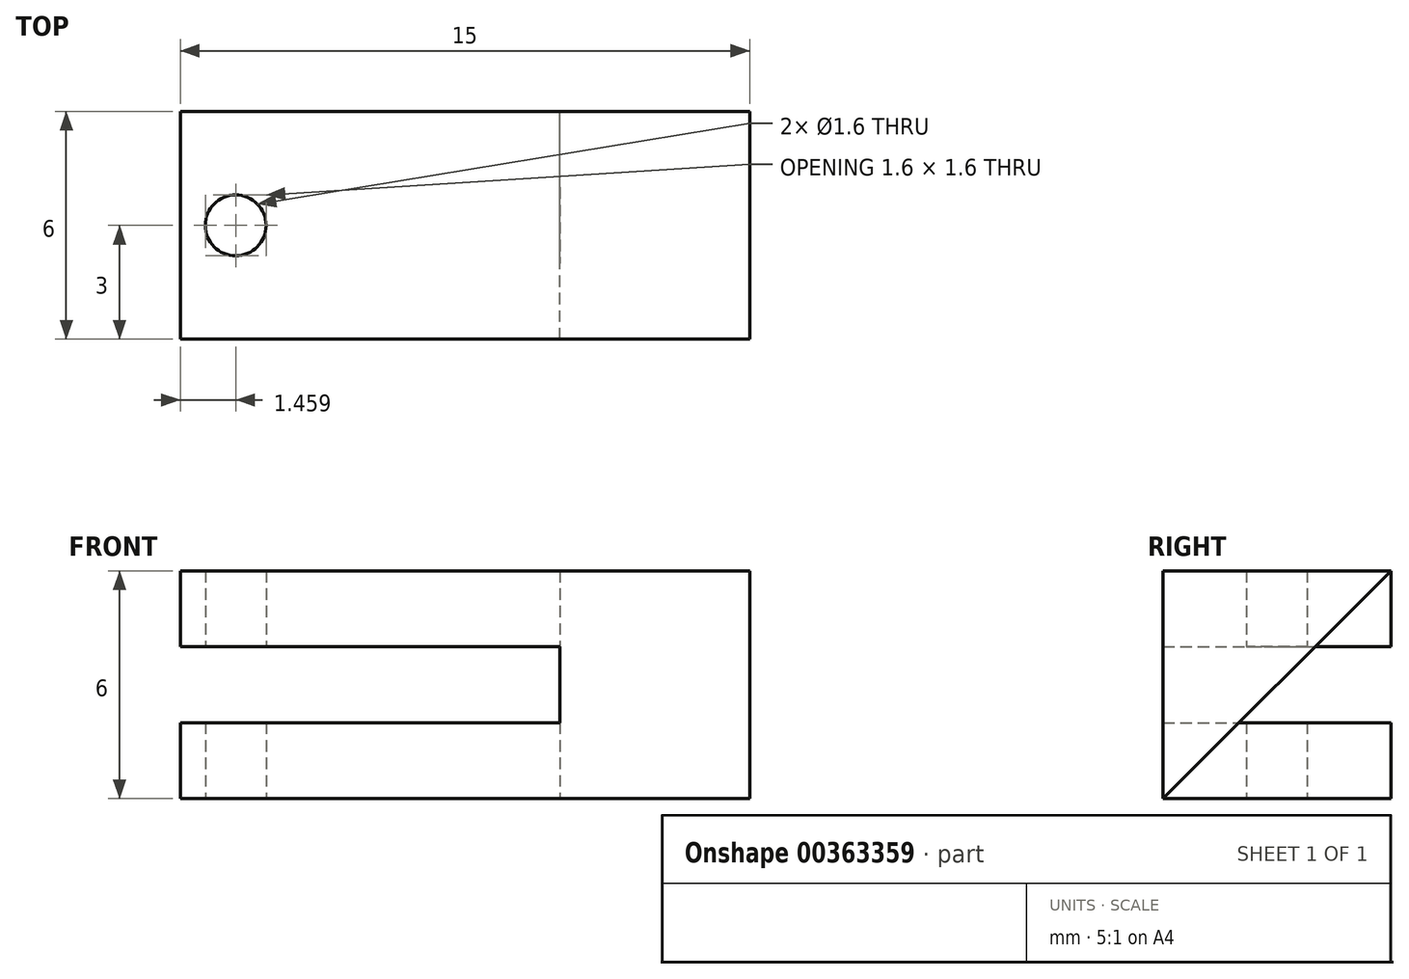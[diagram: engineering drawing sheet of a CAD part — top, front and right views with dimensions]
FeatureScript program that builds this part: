
annotation { "Feature Type Name" : "Feature", "Feature Type Description" : "" }
export const myFeature = defineFeature(function(context is Context, id is Id, definition is map)
    precondition{}
    {
        {
            var Q0;
            Q0=qCreatedBy(makeId("Front.planeOp"),FACE);
            var sketch = newSketch(context, id + "F0", { "sketchPlane" : qUnion([Q0])});
            skLineSegment(sketch, "E0", {"start": v(-77.64, 2.68) * mm, "end": v(-62.64, 2.68) * mm});
            skLineSegment(sketch, "E1", {"start": v(-62.64, 2.68) * mm, "end": v(-62.64, -3.32) * mm});
            skLineSegment(sketch, "E2", {"start": v(-62.64, -3.32) * mm, "end": v(-77.64, -3.32) * mm});
            skLineSegment(sketch, "E3", {"start": v(-77.64, -3.32) * mm, "end": v(-77.64, -1.32) * mm});
            skLineSegment(sketch, "E4", {"start": v(-77.64, -1.32) * mm, "end": v(-67.64, -1.32) * mm});
            skLineSegment(sketch, "E5", {"start": v(-67.64, -1.32) * mm, "end": v(-67.64, 0.68) * mm});
            skLineSegment(sketch, "E6", {"start": v(-67.64, 0.68) * mm, "end": v(-77.64, 0.68) * mm});
            skLineSegment(sketch, "E7", {"start": v(-77.64, 0.68) * mm, "end": v(-77.64, 2.68) * mm});
            skSolve(sketch);
        }
        {
            var Q0;
            Q0=makeQuery(id+"F0.imprint","IMPRINT",FACE,{"disambiguationData":[TD([[makeQuery(id+"F0.imprint","IMPRINT",EDGE,{"derivedFrom":sQuery(id+"F0.wireOp",EDGE,"E0")}),-1.0]])]});
            extrude(context, id + "F1", {"entities" : qUnion([Q0]), "depth" : 6 * mm});
        }
        {
            var Q0;
            Q0=makeQuery(id+"F1.opExtrude","SWEPT_FACE",FACE,{"disambiguationData":[OSD([sQuery(id+"F0.wireOp",EDGE,"E1")])]});
            var sketch = newSketch(context, id + "F2", { "sketchPlane" : qUnion([Q0])});
            skPoint(sketch, "E8.endSnap0", {"position": v(0, -0.32) * mm});
            skLineSegment(sketch, "E9", {"start": v(-6, 2.68) * mm, "end": v(0, -3.32) * mm});
            skLineSegment(sketch, "E10", {"start": v(0, 2.68) * mm, "end": v(-6, -3.32) * mm});
            skCircle(sketch, "E11", {"center": v(-3, -0.32) * mm, "radius": 1.5 * mm});
            skSolve(sketch);
        }
        {
            var Q0;
            {var subQ0=sQuery(id+"F2.wireOp",EDGE,"E10");var subQ1=sQuery(id+"F2.wireOp",EDGE,"E9");var subQ2=makeQuery(id+"F2.imprint","INTERSECT",VERTEX,{"derivedFrom":[subQ1,subQ0]});Q0=makeQuery(id+"F2.imprint","IMPRINT",FACE,{"disambiguationData":[TD([[makeQuery(id+"F2.imprint","IMPRINT",EDGE,{"disambiguationData":[TD([[subQ2,-1.0]])],"derivedFrom":subQ1}),-1.0]])]});}
            var Q1;
            {var subQ0=sQuery(id+"F2.wireOp",EDGE,"E10");var subQ1=sQuery(id+"F2.wireOp",EDGE,"E9");var subQ2=makeQuery(id+"F2.imprint","INTERSECT",VERTEX,{"derivedFrom":[subQ1,subQ0]});Q1=makeQuery(id+"F2.imprint","IMPRINT",FACE,{"disambiguationData":[TD([[makeQuery(id+"F2.imprint","IMPRINT",EDGE,{"disambiguationData":[TD([[subQ2,-1.0]])],"derivedFrom":subQ1}),1.0]])]});}
            var Q2;
            {var subQ0=sQuery(id+"F2.wireOp",EDGE,"E11");var subQ1=sQuery(id+"F2.wireOp",EDGE,"E9");var subQ2=makeQuery(id+"F2.imprint","INTERSECT",VERTEX,{"disambiguationData":[OD(0.0)],"derivedFrom":[subQ1,subQ0]});Q2=makeQuery(id+"F2.imprint","IMPRINT",FACE,{"disambiguationData":[TD([[makeQuery(id+"F2.imprint","IMPRINT",EDGE,{"disambiguationData":[TD([[subQ2,-1.0]])],"derivedFrom":subQ1}),1.0]])]});}
            var Q3;
            {var subQ0=sQuery(id+"F2.wireOp",EDGE,"E11");var subQ1=sQuery(id+"F2.wireOp",EDGE,"E9");var subQ2=makeQuery(id+"F2.imprint","INTERSECT",VERTEX,{"disambiguationData":[OD(0.0)],"derivedFrom":[subQ1,subQ0]});Q3=makeQuery(id+"F2.imprint","IMPRINT",FACE,{"disambiguationData":[TD([[makeQuery(id+"F2.imprint","IMPRINT",EDGE,{"disambiguationData":[TD([[subQ2,-1.0]])],"derivedFrom":subQ1}),-1.0]])]});}
            extrude(context, id + "F3", {"entities" : qUnion([Q0, Q1, Q2, Q3]), "operationType" : NewBodyOperationType.REMOVE, "oppositeDirection" : true, "depth" : 5 * mm});
        }
        {
            var Q0;
            Q0=makeQuery(id+"F1.opExtrude","SWEPT_FACE",FACE,{"disambiguationData":[OSD([sQuery(id+"F0.wireOp",EDGE,"E2")])]});
            var sketch = newSketch(context, id + "F4", { "sketchPlane" : qUnion([Q0])});
            skCircle(sketch, "E12", {"center": v(-76.18, 3) * mm, "radius": 0.8 * mm});
            skPoint(sketch, "E12.centerSnap0", {"position": v(-77.64, 3) * mm});
            skSolve(sketch);
        }
        {
            var Q0;
            Q0=makeQuery(id+"F4.imprint","IMPRINT",FACE,{"disambiguationData":[TD([[makeQuery(id+"F4.imprint","IMPRINT",EDGE,{"derivedFrom":sQuery(id+"F4.wireOp",EDGE,"E12")}),1.0]])]});
            extrude(context, id + "F5", {"entities" : qUnion([Q0]), "operationType" : NewBodyOperationType.REMOVE, "oppositeDirection" : true, "depth" : 25 * mm});
        }
    });
